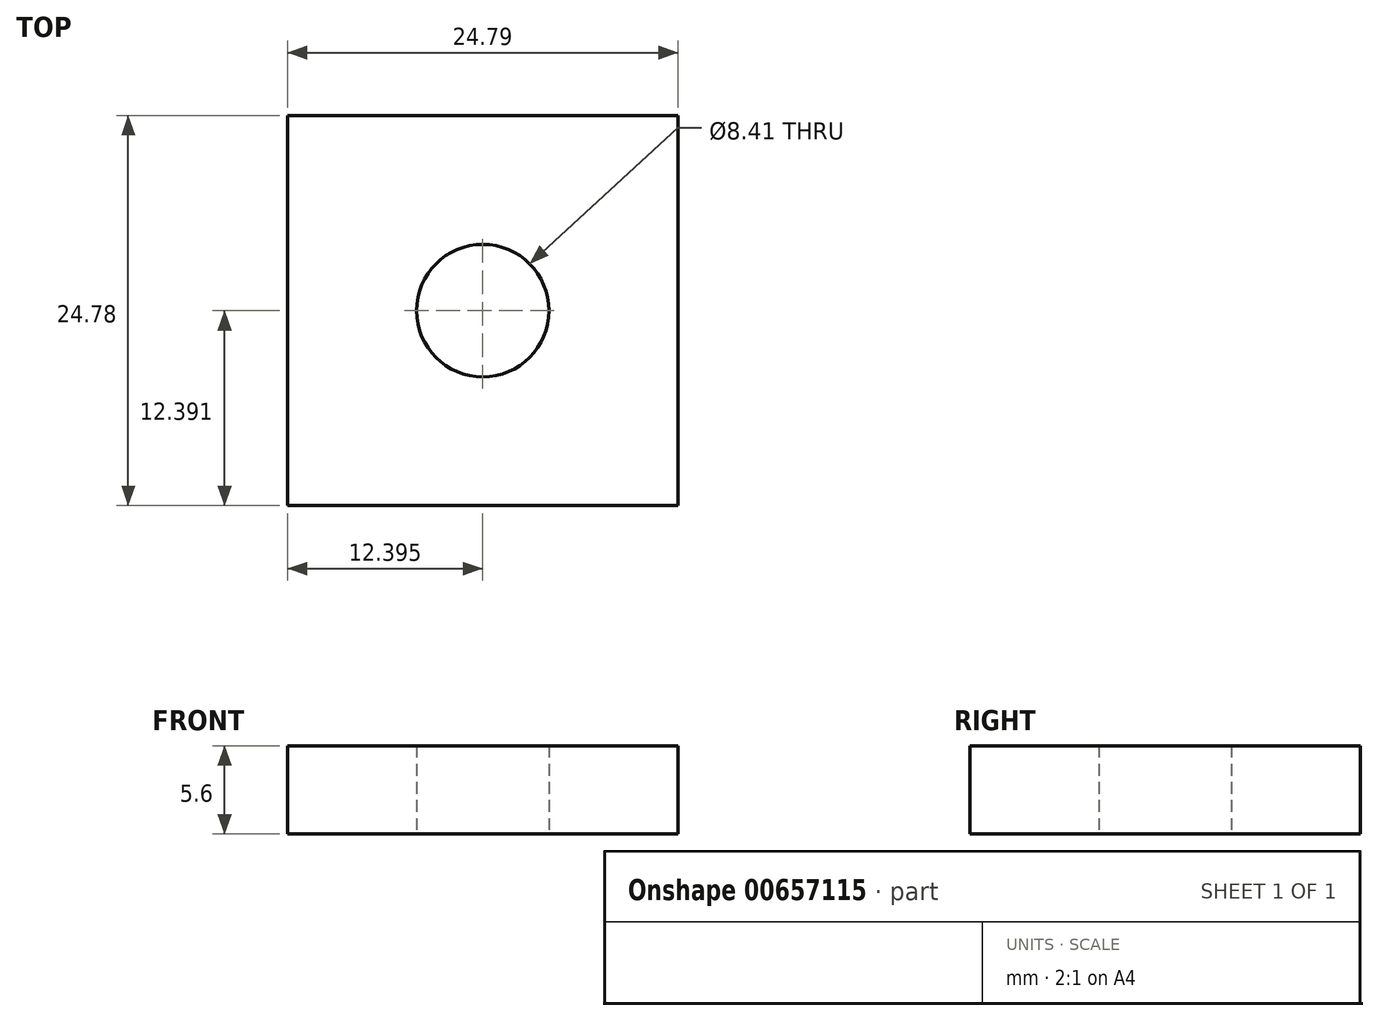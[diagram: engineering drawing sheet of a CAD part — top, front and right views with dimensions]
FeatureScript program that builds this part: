
annotation { "Feature Type Name" : "Feature", "Feature Type Description" : "" }
export const myFeature = defineFeature(function(context is Context, id is Id, definition is map)
    precondition{}
    {
        {
            var Q0;
            Q0=qCreatedBy(makeId("Top.planeOp"),FACE);
            var sketch = newSketch(context, id + "F0", { "sketchPlane" : qUnion([Q0])});
            skLineSegment(sketch, "E0.bottom", {"start": v(-27.24, 14.18) * mm, "end": v(-52.03, 14.18) * mm});
            skLineSegment(sketch, "E0.top", {"start": v(-27.24, 38.96) * mm, "end": v(-52.03, 38.96) * mm});
            skLineSegment(sketch, "E0.left", {"start": v(-27.24, 14.18) * mm, "end": v(-27.24, 38.96) * mm});
            skLineSegment(sketch, "E0.right", {"start": v(-52.03, 14.18) * mm, "end": v(-52.03, 38.96) * mm});
            skPoint(sketch, "E0.middle", {"position": v(-39.64, 26.57) * mm});
            skCircle(sketch, "E1", {"center": v(-39.64, 26.57) * mm, "radius": 4.2 * mm});
            skSolve(sketch);
        }
        {
            var Q0;
            Q0 = qSketchRegion(id + "F0", true);
            extrude(context, id + "F1", {"entities" : qUnion([Q0]), "depth" : 5.6 * mm, "offsetDistance" : 25 * mm});
        }
        {
            var Q0;
            Q0=makeQuery(id+"F1.opExtrude","CAP_FACE",FACE,{"disambiguationData":[OSD([sQuery(id+"F0.wireOp",EDGE,"E0.bottom"),sQuery(id+"F0.wireOp",EDGE,"E0.top"),sQuery(id+"F0.wireOp",EDGE,"E0.left"),sQuery(id+"F0.wireOp",EDGE,"E0.right"),sQuery(id+"F0.wireOp",EDGE,"E1")])],"isStart":false});
            extrude(context, id + "F2", {"entities" : qUnion([Q0]), "operationType" : NewBodyOperationType.ADD, "oppositeDirection" : true, "depth" : 1.6 * mm, "offsetDistance" : 25 * mm});
        }
    });
